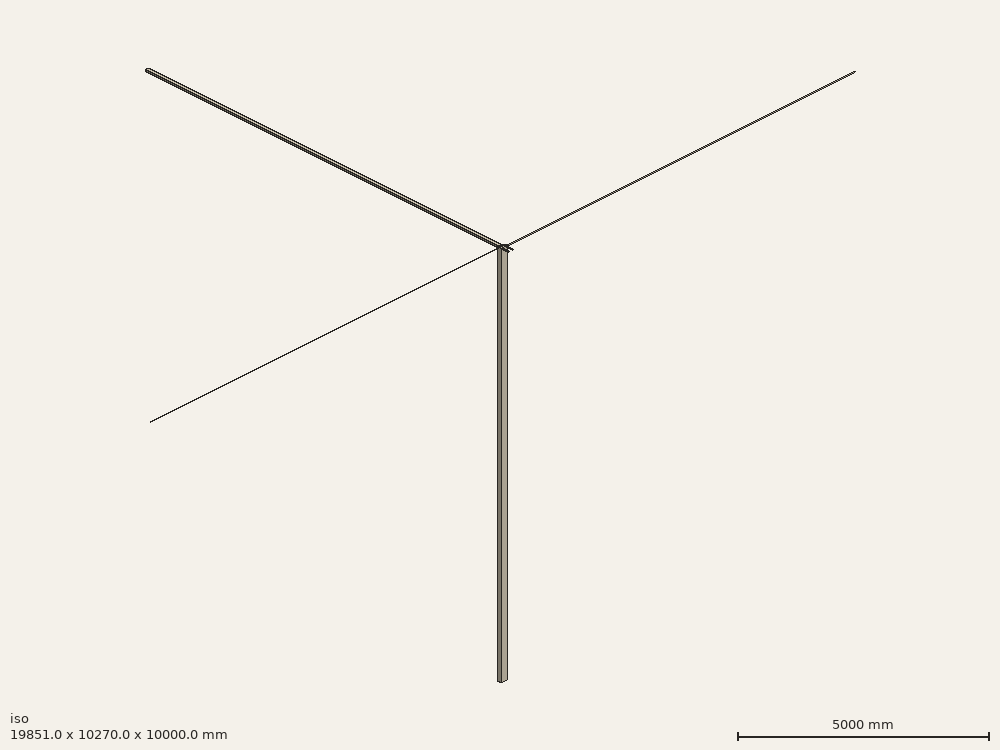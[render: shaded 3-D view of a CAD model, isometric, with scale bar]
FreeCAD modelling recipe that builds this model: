
FCSTD DOCUMENT  (FreeCAD 0.15R4671 (Git))
Label: ZBedBearingCaps
License: All rights reserved
LicenseURL: http://en.wikipedia.org/wiki/All_rights_reserved
objects: Sketcher::SketchObject×27, PartDesign::Pocket×23, Part::Feature×13, Mesh::Feature×9, PartDesign::Pad×4, PartDesign::Chamfer×1, PartDesign::Fillet×1
note: 96 computed .brp shape members not serialized (recipe doc carries the construction recipe); baked Part::Feature solids carry a one-line shape summary decoded from their .brp

FEATURE [Part::Feature] Part__Feature  label="ZRodHolderMiddle001"
  Placement = pos=(0,0,-30) rot=(0,0,1;0rad)
  shape: bbox 156.7 x 50 x 15.66 mm, 189 faces (baked)
FEATURE [Sketcher::SketchObject] Sketch
  sketch-geometry (4):
    g0: LineSegment StartX=-74.5 StartY=-14 StartZ=0 EndX=74.5 EndY=-14 EndZ=0
    g1: LineSegment StartX=74.5 StartY=-14 StartZ=0 EndX=74.5 EndY=-79 EndZ=0
    g2: LineSegment StartX=74.5 StartY=-79 StartZ=0 EndX=-74.5 EndY=-79 EndZ=0
    g3: LineSegment StartX=-74.5 StartY=-79 StartZ=0 EndX=-74.5 EndY=-14 EndZ=0
  constraints (12):
    c: Coincident(g0,g1)
    c: Coincident(g1,g2)
    c: Coincident(g2,g3)
    c: Coincident(g3,g0)
    c: Horizontal(g0)
    c: Horizontal(g2)
    c: Vertical(g1)
    c: Vertical(g3)
    c: DistanceY(g0) = -14
    c: DistanceY(g0,g2) = -65
    c: DistanceX(g-1,g0) = 74.5
    c: DistanceX(g-1,g0) = -74.5
FEATURE [Mesh::Feature] MK2a_Heatbed
  Placement = pos=(0,-185,51.5) rot=(0,0,1;0rad)
FEATURE [Part::Feature] Part__Feature001  label="OB1515_270mm"
  Placement = pos=(-60,-44,42.5) rot=(1,0,0;1.5708rad)
  shape: bbox 15 x 270 x 15 mm, 158 faces (baked)
FEATURE [Part::Feature] Part__Feature002  label="OB1515_270mm001"
  Placement = pos=(60,-44,42.5) rot=(1,0,0;1.5708rad)
  shape: bbox 15 x 270 x 15 mm, 158 faces (baked)
FEATURE [Part::Feature] _mmBrasNut
  Placement = pos=(0,-28.25,40) rot=(0,-1,0;1.5708rad)
  shape: bbox 22 x 22 x 16.42 mm, 29 faces (baked)
FEATURE [Part::Feature] LM8UU_8mm_Linear_Bearing
  Placement = pos=(-60,-28,26) rot=(0,1,0;1.5708rad)
  shape: bbox 15 x 15 x 24 mm, 34 faces (baked)
FEATURE [Part::Feature] LM8UU_8mm_Linear_Bearing001
  Placement = pos=(60,-28,26) rot=(0,1,0;1.5708rad)
  shape: bbox 15 x 15 x 24 mm, 34 faces (baked)
FEATURE [Part::Feature] LM8UU_8mm_Linear_Bearing002
  Placement = pos=(-60,-28,53) rot=(0,1,0;1.5708rad)
  shape: bbox 15 x 15 x 24 mm, 34 faces (baked)
FEATURE [Part::Feature] LM8UU_8mm_Linear_Bearing003
  Placement = pos=(60,-28,53) rot=(0,1,0;1.5708rad)
  shape: bbox 15 x 15 x 24 mm, 34 faces (baked)
FEATURE [PartDesign::Pad] Pad
  Length = 55
  Length2 = 100
  Sketch = -> Sketch
  Type = 0
FEATURE [Sketcher::SketchObject] Sketch001
  Placement = pos=(0,-79,0) rot=(1,0,0;1.5708rad)
  Support = -> Pad [Face3]
  sketch-geometry (8):
    g0: LineSegment StartX=-67.75 StartY=50.25 StartZ=0 EndX=-52.25 EndY=50.25 EndZ=0
    g1: LineSegment StartX=-52.25 StartY=50.25 StartZ=0 EndX=-52.25 EndY=-6 EndZ=0
    g2: LineSegment StartX=-52.25 StartY=-6 StartZ=0 EndX=-67.75 EndY=-6 EndZ=0
    g3: LineSegment StartX=-67.75 StartY=-6 StartZ=0 EndX=-67.75 EndY=50.25 EndZ=0
    g4: LineSegment StartX=52.25 StartY=50.25 StartZ=0 EndX=67.75 EndY=50.25 EndZ=0
    g5: LineSegment StartX=67.75 StartY=50.25 StartZ=0 EndX=67.75 EndY=-6.12629 EndZ=0
    g6: LineSegment StartX=67.75 StartY=-6.12629 StartZ=0 EndX=52.25 EndY=-6.12629 EndZ=0
    g7: LineSegment StartX=52.25 StartY=-6.12629 StartZ=0 EndX=52.25 EndY=50.25 EndZ=0
  constraints (16):
    c: Coincident(g0,g1)
    c: Coincident(g1,g2)
    c: Coincident(g2,g3)
    c: Coincident(g3,g0)
    c: Horizontal(g0)
    c: Horizontal(g2)
    c: Vertical(g1)
    c: Vertical(g3)
    c: Coincident(g4,g5)
    c: Coincident(g5,g6)
    c: Coincident(g6,g7)
    c: Coincident(g7,g4)
    c: Horizontal(g4)
    c: Horizontal(g6)
    c: Vertical(g5)
    c: Vertical(g7)
FEATURE [PartDesign::Pocket] Pocket
  Length = 35
  Sketch = -> Sketch001
  Type = 0
FEATURE [Sketcher::SketchObject] Sketch002
  Placement = pos=(-74.5,0,0) rot=(0.57735,-0.57735,-0.57735;2.0944rad)
  Support = -> Pocket [Face2]
  sketch-geometry (5):
    g0: LineSegment StartX=79.5 StartY=35 StartZ=0 EndX=79 EndY=35 EndZ=0
    g1: LineSegment StartX=79 StartY=35 StartZ=0 EndX=44 EndY=0 EndZ=0
    g2: LineSegment StartX=44 StartY=0 StartZ=0 EndX=44 EndY=-0.5 EndZ=0
    g3: LineSegment StartX=44 StartY=-0.5 StartZ=0 EndX=79.5 EndY=-0.5 EndZ=0
    g4: LineSegment StartX=79.5 StartY=-0.5 StartZ=0 EndX=79.5 EndY=35 EndZ=0
  constraints (10):
    c: Horizontal(g0)
    c: Coincident(g0,g1)
    c: PointOnObject(g1,g-1)
    c: Coincident(g1,g2)
    c: Vertical(g2)
    c: Coincident(g2,g3)
    c: Horizontal(g3)
    c: Coincident(g3,g4)
    c: Coincident(g4,g0)
    c: Vertical(g4)
FEATURE [PartDesign::Pocket] Pocket001
  Length = 5
  Sketch = -> Sketch002
  Type = 1
FEATURE [Sketcher::SketchObject] Sketch003
  Placement = pos=(0,-79,0) rot=(1,0,0;1.5708rad)
  Support = -> Pocket001 [Face7]
  sketch-geometry (4):
    g0: LineSegment StartX=-45 StartY=45 StartZ=0 EndX=45 EndY=45 EndZ=0
    g1: LineSegment StartX=45 StartY=45 StartZ=0 EndX=45 EndY=-2 EndZ=0
    g2: LineSegment StartX=45 StartY=-2 StartZ=0 EndX=-45 EndY=-2 EndZ=0
    g3: LineSegment StartX=-45 StartY=-2 StartZ=0 EndX=-45 EndY=45 EndZ=0
  constraints (8):
    c: Coincident(g0,g1)
    c: Coincident(g1,g2)
    c: Coincident(g2,g3)
    c: Coincident(g3,g0)
    c: Horizontal(g0)
    c: Horizontal(g2)
    c: Vertical(g1)
    c: Vertical(g3)
FEATURE [PartDesign::Pocket] Pocket002
  Length = 35
  Sketch = -> Sketch003
  Type = 0
FEATURE [Sketcher::SketchObject] Sketch005
  Placement = pos=(0,-44,0) rot=(1,0,0;1.5708rad)
  Support = -> Pocket002 [Face13]
  sketch-geometry (4):
    g0: LineSegment StartX=-45 StartY=45 StartZ=0 EndX=45 EndY=45 EndZ=0
    g1: LineSegment StartX=45 StartY=45 StartZ=0 EndX=45 EndY=-2 EndZ=0
    g2: LineSegment StartX=45 StartY=-2 StartZ=0 EndX=-45 EndY=-2 EndZ=0
    g3: LineSegment StartX=-45 StartY=-2 StartZ=0 EndX=-45 EndY=45 EndZ=0
  constraints (8):
    c: Coincident(g0,g1)
    c: Coincident(g1,g2)
    c: Coincident(g2,g3)
    c: Coincident(g3,g0)
    c: Horizontal(g0)
    c: Horizontal(g2)
    c: Vertical(g1)
    c: Vertical(g3)
FEATURE [PartDesign::Pocket] Pocket003
  Length = 5
  Sketch = -> Sketch005
  Type = 1
FEATURE [Sketcher::SketchObject] Sketch006
  Placement = pos=(0,0,55) rot=(0,0,1;0rad)
  Support = -> Pocket003 [Face5]
  sketch-geometry (4):
    g0: LineSegment StartX=-45 StartY=-81 StartZ=0 EndX=-45 EndY=-44 EndZ=0
    g1: LineSegment StartX=-45 StartY=-44 StartZ=0 EndX=45 EndY=-44 EndZ=0
    g2: LineSegment StartX=45 StartY=-44 StartZ=0 EndX=45 EndY=-81 EndZ=0
    g3: LineSegment StartX=45 StartY=-81 StartZ=0 EndX=-45 EndY=-81 EndZ=0
  constraints (4):
    c: Coincident(g0,g1)
    c: Coincident(g1,g2)
    c: Coincident(g2,g3)
    c: Coincident(g3,g0)
FEATURE [PartDesign::Pocket] Pocket004
  Length = 5
  Sketch = -> Sketch006
  Type = 1
FEATURE [Sketcher::SketchObject] Sketch007
  Placement = pos=(0,0,55) rot=(0,0,1;0rad)
  Support = -> Pocket004 [Face6]
  sketch-geometry (1):
    g0: Circle CenterX=0 CenterY=-28.2788 CenterZ=0 NormalX=0 NormalY=0 NormalZ=1 Radius=5.50059
FEATURE [PartDesign::Pocket] Pocket005
  Length = 5
  Sketch = -> Sketch007
  Type = 1
FEATURE [Sketcher::SketchObject] Sketch008
  Placement = pos=(0,0,55) rot=(0,0,1;0rad)
  Support = -> Pocket005 [Face8]
  sketch-geometry (4):
    g0: Circle CenterX=0 CenterY=-36.25 CenterZ=0 NormalX=0 NormalY=0 NormalZ=1 Radius=1.5
    g1: Circle CenterX=0 CenterY=-20.25 CenterZ=0 NormalX=0 NormalY=0 NormalZ=1 Radius=1.5
    g2: Circle CenterX=8 CenterY=-28.25 CenterZ=0 NormalX=0 NormalY=0 NormalZ=1 Radius=1.5
    g3: Circle CenterX=-8 CenterY=-28.25 CenterZ=0 NormalX=0 NormalY=0 NormalZ=1 Radius=1.5
  constraints (4):
    c: Radius(g3) = 1.5
    c: Equal(g3,g1)
    c: Equal(g3,g2)
    c: Equal(g3,g0)
FEATURE [PartDesign::Pocket] Pocket006
  Length = 5
  Sketch = -> Sketch008
  Type = 1
FEATURE [Sketcher::SketchObject] Sketch009
  Placement = pos=(0,0,55) rot=(0,0,1;0rad)
  Support = -> Pocket006 [Face8]
  sketch-geometry (2):
    g0: Circle CenterX=60 CenterY=-28 CenterZ=0 NormalX=0 NormalY=0 NormalZ=1 Radius=7.75
    g1: Circle CenterX=-60 CenterY=-28 CenterZ=0 NormalX=0 NormalY=0 NormalZ=1 Radius=7.75
  constraints (2):
    c: Radius(g1) = 7.75
    c: Equal(g1,g0)
FEATURE [PartDesign::Pocket] Pocket007
  Length = 26.75
  Sketch = -> Sketch009
  Type = 0
FEATURE [Sketcher::SketchObject] Sketch010
  Placement = pos=(0,0,0) rot=(1,0,0;3.14159rad)
  Support = -> Pocket007 [Face2]
  sketch-geometry (2):
    g0: Circle CenterX=-60 CenterY=28 CenterZ=0 NormalX=0 NormalY=0 NormalZ=1 Radius=7.75
    g1: Circle CenterX=60 CenterY=28 CenterZ=0 NormalX=0 NormalY=0 NormalZ=1 Radius=7.75
  constraints (2):
    c: Radius(g0) = 7.75
    c: Equal(g0,g1)
FEATURE [PartDesign::Pocket] Pocket008
  Length = 26.75
  Sketch = -> Sketch010
  Type = 0
FEATURE [Sketcher::SketchObject] Sketch011
  Placement = pos=(0,0,0) rot=(1,0,0;3.14159rad)
  Support = -> Pocket008 [Face2]
  sketch-geometry (8):
    g0: LineSegment StartX=50 StartY=38 StartZ=0 EndX=70 EndY=38 EndZ=0
    g1: LineSegment StartX=70 StartY=38 StartZ=0 EndX=70 EndY=18 EndZ=0
    g2: LineSegment StartX=70 StartY=18 StartZ=0 EndX=50 EndY=18 EndZ=0
    g3: LineSegment StartX=50 StartY=18 StartZ=0 EndX=50 EndY=38 EndZ=0
    g4: LineSegment StartX=-50 StartY=38 StartZ=0 EndX=-70 EndY=38 EndZ=0
    g5: LineSegment StartX=-70 StartY=38 StartZ=0 EndX=-70 EndY=17.9245 EndZ=0
    g6: LineSegment StartX=-70 StartY=17.9245 StartZ=0 EndX=-50 EndY=17.9245 EndZ=0
    g7: LineSegment StartX=-50 StartY=17.9245 StartZ=0 EndX=-50 EndY=38 EndZ=0
  constraints (16):
    c: Coincident(g0,g1)
    c: Coincident(g1,g2)
    c: Coincident(g2,g3)
    c: Coincident(g3,g0)
    c: Horizontal(g0)
    c: Horizontal(g2)
    c: Vertical(g1)
    c: Vertical(g3)
    c: Coincident(g4,g5)
    c: Coincident(g5,g6)
    c: Coincident(g6,g7)
    c: Coincident(g7,g4)
    c: Horizontal(g4)
    c: Horizontal(g6)
    c: Vertical(g5)
    c: Vertical(g7)
FEATURE [PartDesign::Pad] Pad001
  Length = 1.25
  Length2 = 100
  Reversed = true
  Sketch = -> Sketch011
  Type = 0
FEATURE [Sketcher::SketchObject] Sketch012
  Placement = pos=(0,0,55) rot=(0,0,1;0rad)
  Support = -> Pad001 [Face6]
  sketch-geometry (8):
    g0: LineSegment StartX=-50 StartY=-18 StartZ=0 EndX=-70 EndY=-18 EndZ=0
    g1: LineSegment StartX=-70 StartY=-18 StartZ=0 EndX=-70 EndY=-38 EndZ=0
    g2: LineSegment StartX=-70 StartY=-38 StartZ=0 EndX=-50 EndY=-38 EndZ=0
    g3: LineSegment StartX=-50 StartY=-38 StartZ=0 EndX=-50 EndY=-18 EndZ=0
    g4: LineSegment StartX=50 StartY=-18 StartZ=0 EndX=70 EndY=-18 EndZ=0
    g5: LineSegment StartX=70 StartY=-18 StartZ=0 EndX=70 EndY=-38 EndZ=0
    g6: LineSegment StartX=70 StartY=-38 StartZ=0 EndX=50 EndY=-38 EndZ=0
    g7: LineSegment StartX=50 StartY=-38 StartZ=0 EndX=50 EndY=-18 EndZ=0
  constraints (16):
    c: Coincident(g0,g1)
    c: Coincident(g1,g2)
    c: Coincident(g2,g3)
    c: Coincident(g3,g0)
    c: Horizontal(g0)
    c: Horizontal(g2)
    c: Vertical(g1)
    c: Vertical(g3)
    c: Coincident(g4,g5)
    c: Coincident(g5,g6)
    c: Coincident(g6,g7)
    c: Coincident(g7,g4)
    c: Horizontal(g4)
    c: Horizontal(g6)
    c: Vertical(g5)
    c: Vertical(g7)
FEATURE [PartDesign::Pad] Pad002
  Length = 1.25
  Length2 = 100
  Reversed = true
  Sketch = -> Sketch012
  Type = 0
FEATURE [Part::Feature] Pad002001  label="Pad003"
  shape: bbox 149 x 65 x 55 mm, 41 faces (baked)
FEATURE [Sketcher::SketchObject] Sketch013
  Placement = pos=(0,0,55) rot=(0,0,1;0rad)
  Support = -> Pad002001 [Face29]
  sketch-geometry (2):
    g0: Circle CenterX=60 CenterY=-28 CenterZ=0 NormalX=0 NormalY=0 NormalZ=1 Radius=6
    g1: Circle CenterX=-60 CenterY=-28 CenterZ=0 NormalX=0 NormalY=0 NormalZ=1 Radius=6
  constraints (2):
    c: Radius(g0) = 6
    c: Equal(g0,g1)
FEATURE [PartDesign::Pocket] Pocket009
  Length = 5
  Sketch = -> Sketch013
  Type = 1
FEATURE [Mesh::Feature] HexNutStyle1_M3
  Placement = pos=(-47,-148,15) rot=(-0.935113,0.250563,0.250563;1.63783rad)
FEATURE [Mesh::Feature] HexNutStyle1_M
  Placement = pos=(-70,-148,15) rot=(-0.935113,0.250563,0.250563;1.63783rad)
FEATURE [Mesh::Feature] HexNutStyle1_M004
  Placement = pos=(72.5,-148,15) rot=(-0.935113,0.250563,0.250563;1.63783rad)
FEATURE [Mesh::Feature] HexNutStyle1_M005
  Placement = pos=(49.5,-148,15) rot=(-0.935113,0.250563,0.250563;1.63783rad)
FEATURE [Mesh::Feature] HexNutStyle1_M006
  Placement = pos=(-47,-148,-12) rot=(-0.935113,0.250563,0.250563;1.63783rad)
FEATURE [Mesh::Feature] HexNutStyle1_M007
  Placement = pos=(-70,-148,-12) rot=(-0.935113,0.250563,0.250563;1.63783rad)
FEATURE [Mesh::Feature] HexNutStyle1_M008
  Placement = pos=(72.5,-148,-12) rot=(-0.935113,0.250563,0.250563;1.63783rad)
FEATURE [Mesh::Feature] HexNutStyle1_M009
  Placement = pos=(49.5,-148,-12) rot=(-0.935113,0.250563,0.250563;1.63783rad)
FEATURE [Sketcher::SketchObject] Sketch014
  Placement = pos=(0,-14,0) rot=(0,0.707107,0.707107;3.14159rad)
  Support = -> Pocket009 [Face1]
  sketch-geometry (8):
    g0: Circle CenterX=48.3004 CenterY=41.1597 CenterZ=0 NormalX=0 NormalY=0 NormalZ=1 Radius=1.8
    g1: Circle CenterX=71.3061 CenterY=41.157 CenterZ=0 NormalX=0 NormalY=0 NormalZ=1 Radius=1.8
    g2: Circle CenterX=71.2993 CenterY=14.1443 CenterZ=0 NormalX=0 NormalY=0 NormalZ=1 Radius=1.8
    g3: Circle CenterX=48.2996 CenterY=14.1465 CenterZ=0 NormalX=0 NormalY=0 NormalZ=1 Radius=1.8
    g4: Circle CenterX=-48.2006 CenterY=41.1589 CenterZ=0 NormalX=0 NormalY=0 NormalZ=1 Radius=1.8
    g5: Circle CenterX=-71.2074 CenterY=41.1588 CenterZ=0 NormalX=0 NormalY=0 NormalZ=1 Radius=1.8
    g6: Circle CenterX=-48.2029 CenterY=14.1601 CenterZ=0 NormalX=0 NormalY=0 NormalZ=1 Radius=1.8
    g7: Circle CenterX=-71.1962 CenterY=14.1573 CenterZ=0 NormalX=0 NormalY=0 NormalZ=1 Radius=1.8
  constraints (2):
    c: Radius(g0) = 1.8
    c: Equal(g0, g1-g7) x7
FEATURE [PartDesign::Pocket] Pocket010
  Length = 28
  Sketch = -> Sketch014
  Type = 0
FEATURE [Sketcher::SketchObject] Sketch017
  Placement = pos=(0,0,55) rot=(0,0,1;0rad)
  Support = -> Pocket010 [Face5]
  sketch-geometry (21):
    g0: LineSegment StartX=74 StartY=-43.5 StartZ=0 EndX=74.5 EndY=-44 EndZ=0
    g1: LineSegment StartX=74.5 StartY=-44 StartZ=0 EndX=76.5 EndY=-42 EndZ=0
    g2: LineSegment StartX=76.5 StartY=-42 StartZ=0 EndX=76.5 EndY=-14 EndZ=0
    g3: LineSegment StartX=76.5 StartY=-14 StartZ=0 EndX=74 EndY=-14 EndZ=0
    g4: LineSegment StartX=74 StartY=-14 StartZ=0 EndX=74 EndY=-43.1086 EndZ=0
    g5: LineSegment StartX=74 StartY=-43.1086 StartZ=0 EndX=74 EndY=-43.5 EndZ=0
    g6: LineSegment StartX=-74 StartY=-44 StartZ=0 EndX=-74.5 EndY=-44 EndZ=0
    g7: LineSegment StartX=-74.5 StartY=-44 StartZ=0 EndX=-76.5 EndY=-42 EndZ=0
    g8: LineSegment StartX=-76.5 StartY=-42 StartZ=0 EndX=-76.5 EndY=-14 EndZ=0
    g9: LineSegment StartX=-76.5 StartY=-14 StartZ=0 EndX=-74 EndY=-14 EndZ=0
    g10: LineSegment StartX=-74 StartY=-14 StartZ=0 EndX=-74 EndY=-44 EndZ=0
    g11: LineSegment StartX=-45.5 StartY=-44 StartZ=0 EndX=-45 EndY=-44 EndZ=0
    g12: LineSegment StartX=-45 StartY=-44 StartZ=0 EndX=-43 EndY=-42 EndZ=0
    g13: LineSegment StartX=-43 StartY=-42 StartZ=0 EndX=-43 EndY=-14 EndZ=0
    g14: LineSegment StartX=-43 StartY=-14 StartZ=0 EndX=-45.5 EndY=-14 EndZ=0
    g15: LineSegment StartX=-45.5 StartY=-14 StartZ=0 EndX=-45.5 EndY=-44 EndZ=0
    g16: LineSegment StartX=45.5 StartY=-44 StartZ=0 EndX=45 EndY=-44 EndZ=0
    g17: LineSegment StartX=45 StartY=-44 StartZ=0 EndX=43 EndY=-42 EndZ=0
    g18: LineSegment StartX=43 StartY=-42 StartZ=0 EndX=43 EndY=-14 EndZ=0
    g19: LineSegment StartX=43 StartY=-14 StartZ=0 EndX=45.5 EndY=-14 EndZ=0
    g20: LineSegment StartX=45.5 StartY=-14 StartZ=0 EndX=45.5 EndY=-44 EndZ=0
  constraints (21):
    c: Coincident(g0,g1)
    c: Coincident(g1,g2)
    c: Coincident(g2,g3)
    c: Coincident(g3,g4)
    c: Coincident(g4,g5)
    c: Coincident(g5,g0)
    c: Coincident(g6,g7)
    c: Coincident(g7,g8)
    c: Coincident(g8,g9)
    c: Coincident(g9,g10)
    c: Coincident(g10,g6)
    c: Coincident(g11,g12)
    c: Coincident(g12,g13)
    c: Coincident(g13,g14)
    c: Coincident(g14,g15)
    c: Coincident(g15,g11)
    c: Coincident(g16,g17)
    c: Coincident(g17,g18)
    c: Coincident(g18,g19)
    c: Coincident(g19,g20)
    c: Coincident(g20,g16)
FEATURE [PartDesign::Pad] Pad002002
  Length = 55
  Length2 = 100
  Reversed = true
  Sketch = -> Sketch017
  Type = 0
FEATURE [Part::Feature] Pad002003
  shape: bbox 153 x 65 x 55 mm, 71 faces (baked)
FEATURE [Sketcher::SketchObject] Sketch018
  Placement = pos=(0,-14,0) rot=(0,0.707107,0.707107;3.14159rad)
  Support = -> Pad002003 [Face34]
  sketch-geometry (8):
    g0: Circle CenterX=-71.1996 CenterY=41.1697 CenterZ=0 NormalX=0 NormalY=0 NormalZ=1 Radius=3.4
    g1: Circle CenterX=-48.1947 CenterY=41.1566 CenterZ=0 NormalX=0 NormalY=0 NormalZ=1 Radius=3.4
    g2: Circle CenterX=-71.196 CenterY=14.1515 CenterZ=0 NormalX=0 NormalY=0 NormalZ=1 Radius=3.4
    g3: Circle CenterX=-48.1951 CenterY=14.1668 CenterZ=0 NormalX=0 NormalY=0 NormalZ=1 Radius=3.4
    g4: Circle CenterX=48.2953 CenterY=41.166 CenterZ=0 NormalX=0 NormalY=0 NormalZ=1 Radius=3.4
    g5: Circle CenterX=71.309 CenterY=41.1689 CenterZ=0 NormalX=0 NormalY=0 NormalZ=1 Radius=3.4
    g6: Circle CenterX=71.2966 CenterY=14.1495 CenterZ=0 NormalX=0 NormalY=0 NormalZ=1 Radius=3.4
    g7: Circle CenterX=48.296 CenterY=14.1509 CenterZ=0 NormalX=0 NormalY=0 NormalZ=1 Radius=3.4
  constraints (2):
    c: Radius(g0) = 3.4
    c: Equal(g0, g1-g7) x7
FEATURE [PartDesign::Pocket] Pocket011
  Length = 12
  Sketch = -> Sketch018
  Type = 0
FEATURE [Sketcher::SketchObject] Sketch019
  Placement = pos=(0,0,55) rot=(0,0,1;0rad)
  Support = -> Pocket011 [Face11]
  sketch-geometry (6):
    g0: LineSegment StartX=-43 StartY=-12 StartZ=0 EndX=-43 EndY=-28 EndZ=0
    g1: LineSegment StartX=-43 StartY=-28 StartZ=0 EndX=-14 EndY=-28 EndZ=0
    g2: ArcOfCircle CenterX=0 CenterY=-28 CenterZ=0 NormalX=0 NormalY=0 NormalZ=1 Radius=14 StartAngle=0 EndAngle=3.14159
    g3: LineSegment StartX=-43 StartY=-12 StartZ=0 EndX=43 EndY=-12 EndZ=0
    g4: LineSegment StartX=43 StartY=-12 StartZ=0 EndX=43 EndY=-28 EndZ=0
    g5: LineSegment StartX=43 StartY=-28 StartZ=0 EndX=14 EndY=-28 EndZ=0
  constraints (6):
    c: Coincident(g0,g1)
    c: Coincident(g1,g2)
    c: Coincident(g3,g4)
    c: Coincident(g4,g5)
    c: Coincident(g2,g5)
    c: Coincident(g0,g3)
FEATURE [PartDesign::Pocket] Pocket012
  Length = 5
  Sketch = -> Sketch019
  Type = 1
FEATURE [PartDesign::Chamfer] Chamfer
  Base = -> Pocket012 [Edge138,Edge141]
  Size = 11
FEATURE [Sketcher::SketchObject] Sketch020
  Placement = pos=(0,0,55) rot=(0,0,1;0rad)
  Support = -> Chamfer [Face9]
  sketch-geometry (20):
    g0: LineSegment StartX=41 StartY=-16 StartZ=0 EndX=43 EndY=-16 EndZ=0
    g1: LineSegment StartX=43 StartY=-16 StartZ=0 EndX=45 EndY=-14 EndZ=0
    g2: LineSegment StartX=45 StartY=-14 StartZ=0 EndX=45 EndY=-12 EndZ=0
    g3: LineSegment StartX=45 StartY=-12 StartZ=0 EndX=41 EndY=-12 EndZ=0
    g4: LineSegment StartX=41 StartY=-12 StartZ=0 EndX=41 EndY=-16 EndZ=0
    g5: LineSegment StartX=74.5004 StartY=-12 StartZ=0 EndX=74.5004 EndY=-14 EndZ=0
    g6: LineSegment StartX=74.5004 StartY=-14 StartZ=0 EndX=76.5 EndY=-16 EndZ=0
    g7: LineSegment StartX=76.5 StartY=-16 StartZ=0 EndX=78 EndY=-16 EndZ=0
    g8: LineSegment StartX=78 StartY=-16 StartZ=0 EndX=78 EndY=-12 EndZ=0
    g9: LineSegment StartX=78 StartY=-12 StartZ=0 EndX=74.5004 EndY=-12 EndZ=0
    g10: LineSegment StartX=-45 StartY=-13.5 StartZ=0 EndX=-45 EndY=-14 EndZ=0
    g11: LineSegment StartX=-45 StartY=-14 StartZ=0 EndX=-43 EndY=-16 EndZ=0
    g12: LineSegment StartX=-43 StartY=-16 StartZ=0 EndX=-42.5 EndY=-16 EndZ=0
    g13: LineSegment StartX=-42.5 StartY=-16 StartZ=0 EndX=-42.5 EndY=-13.5 EndZ=0
    g14: LineSegment StartX=-42.5 StartY=-13.5 StartZ=0 EndX=-45 EndY=-13.5 EndZ=0
    g15: LineSegment StartX=-77.5 StartY=-13 StartZ=0 EndX=-74.5 EndY=-13 EndZ=0
    g16: LineSegment StartX=-74.5 StartY=-13 StartZ=0 EndX=-74.5 EndY=-14 EndZ=0
    g17: LineSegment StartX=-74.5 StartY=-14 StartZ=0 EndX=-76.5 EndY=-16 EndZ=0
    g18: LineSegment StartX=-76.5 StartY=-16 StartZ=0 EndX=-77.5 EndY=-16 EndZ=0
    g19: LineSegment StartX=-77.5 StartY=-16 StartZ=0 EndX=-77.5 EndY=-13 EndZ=0
  constraints (20):
    c: Coincident(g0,g1)
    c: Coincident(g1,g2)
    c: Coincident(g2,g3)
    c: Coincident(g3,g4)
    c: Coincident(g4,g0)
    c: Coincident(g5,g6)
    c: Coincident(g6,g7)
    c: Coincident(g7,g8)
    c: Coincident(g8,g9)
    c: Coincident(g9,g5)
    c: Coincident(g10,g11)
    c: Coincident(g11,g12)
    c: Coincident(g12,g13)
    c: Coincident(g13,g14)
    c: Coincident(g14,g10)
    c: Coincident(g15,g16)
    c: Coincident(g16,g17)
    c: Coincident(g17,g18)
    c: Coincident(g18,g19)
    c: Coincident(g19,g15)
FEATURE [PartDesign::Pocket] Pocket013
  Length = 5
  Sketch = -> Sketch020
  Type = 1
FEATURE [Sketcher::SketchObject] Sketch021
  Placement = pos=(0,0,55) rot=(0,0,1;0rad)
  Support = -> Pocket013 [Face8]
  sketch-geometry (4):
    g0: Circle CenterX=60 CenterY=-72.5 CenterZ=0 NormalX=0 NormalY=0 NormalZ=1 Radius=1.8
    g1: Circle CenterX=-60 CenterY=-72.5 CenterZ=0 NormalX=0 NormalY=0 NormalZ=1 Radius=1.8
    g2: Circle CenterX=-60 CenterY=-50 CenterZ=0 NormalX=0 NormalY=0 NormalZ=1 Radius=1.8
    g3: Circle CenterX=60 CenterY=-50 CenterZ=0 NormalX=0 NormalY=0 NormalZ=1 Radius=1.8
  constraints (4):
    c: Radius(g0) = 1.8
    c: Equal(g0,g1)
    c: Equal(g0,g2)
    c: Equal(g0,g3)
FEATURE [PartDesign::Pocket] Pocket014
  Length = 5
  Sketch = -> Sketch021
  Type = 1
FEATURE [Sketcher::SketchObject] Sketch022
  Placement = pos=(0,0,55) rot=(0,0,1;0rad)
  Support = -> Pocket014 [Face8]
  sketch-geometry (4):
    g0: Circle CenterX=60 CenterY=-50 CenterZ=0 NormalX=0 NormalY=0 NormalZ=1 Radius=3.6
    g1: Circle CenterX=60 CenterY=-72.5 CenterZ=0 NormalX=0 NormalY=0 NormalZ=1 Radius=3.6
    g2: Circle CenterX=-60 CenterY=-50 CenterZ=0 NormalX=0 NormalY=0 NormalZ=1 Radius=3.6
    g3: Circle CenterX=-60 CenterY=-72.5 CenterZ=0 NormalX=0 NormalY=0 NormalZ=1 Radius=3.6
  constraints (4):
    c: Radius(g0) = 3.6
    c: Equal(g0,g1)
    c: Equal(g0,g2)
    c: Equal(g0,g3)
FEATURE [PartDesign::Pocket] Pocket015
  Length = 3
  Sketch = -> Sketch022
  Type = 0
FEATURE [Sketcher::SketchObject] Sketch023
  Placement = pos=(74.5,0,0) rot=(0.57735,0.57735,0.57735;2.0944rad)
  Support = -> Pocket015 [Face35]
  sketch-geometry (2):
    g0: Circle CenterX=-72.5 CenterY=42.5 CenterZ=0 NormalX=0 NormalY=0 NormalZ=1 Radius=1.8
    g1: Circle CenterX=-50 CenterY=42.5 CenterZ=0 NormalX=0 NormalY=0 NormalZ=1 Radius=1.8
  constraints (2):
    c: Radius(g0) = 1.8
    c: Equal(g0,g1)
FEATURE [PartDesign::Pocket] Pocket016
  Length = 5
  Sketch = -> Sketch023
  Type = 1
FEATURE [Sketcher::SketchObject] Sketch024
  Placement = pos=(74.5,0,0) rot=(0.57735,0.57735,0.57735;2.0944rad)
  Support = -> Pocket016 [Face37]
  sketch-geometry (2):
    g0: Circle CenterX=-50 CenterY=42.5 CenterZ=0 NormalX=0 NormalY=0 NormalZ=1 Radius=3.6
    g1: Circle CenterX=-72.5 CenterY=42.5 CenterZ=0 NormalX=0 NormalY=0 NormalZ=1 Radius=3.6
  constraints (2):
    c: Radius(g1) = 3.6
    c: Equal(g1,g0)
FEATURE [PartDesign::Pocket] Pocket017
  Length = 3
  Sketch = -> Sketch024
  Type = 0
FEATURE [Sketcher::SketchObject] Sketch025
  Placement = pos=(45,0,0) rot=(0.57735,-0.57735,-0.57735;2.0944rad)
  Support = -> Pocket017 [Face33]
  sketch-geometry (2):
    g0: Circle CenterX=50 CenterY=42.5 CenterZ=0 NormalX=0 NormalY=0 NormalZ=1 Radius=3.6
    g1: Circle CenterX=72.5 CenterY=42.5 CenterZ=0 NormalX=0 NormalY=0 NormalZ=1 Radius=3.6
  constraints (2):
    c: Radius(g0) = 3.6
    c: Equal(g0,g1)
FEATURE [PartDesign::Pocket] Pocket018
  Length = 3
  Sketch = -> Sketch025
  Type = 0
FEATURE [Sketcher::SketchObject] Sketch026
  Placement = pos=(-45,0,0) rot=(0.57735,0.57735,0.57735;2.0944rad)
  Support = -> Pocket018 [Face6]
  sketch-geometry (2):
    g0: Circle CenterX=-50 CenterY=42.5 CenterZ=0 NormalX=0 NormalY=0 NormalZ=1 Radius=3.6
    g1: Circle CenterX=-72.5 CenterY=42.5 CenterZ=0 NormalX=0 NormalY=0 NormalZ=1 Radius=3.6
  constraints (2):
    c: Radius(g0) = 3.6
    c: Equal(g0,g1)
FEATURE [PartDesign::Pocket] Pocket019
  Length = 3
  Sketch = -> Sketch026
  Type = 0
FEATURE [Sketcher::SketchObject] Sketch027
  Placement = pos=(-74.5,0,0) rot=(0.57735,-0.57735,-0.57735;2.0944rad)
  Support = -> Pocket019 [Face31]
  sketch-geometry (2):
    g0: Circle CenterX=50 CenterY=42.5 CenterZ=0 NormalX=0 NormalY=0 NormalZ=1 Radius=3.6
    g1: Circle CenterX=72.5 CenterY=42.5 CenterZ=0 NormalX=0 NormalY=0 NormalZ=1 Radius=3.6
  constraints (2):
    c: Radius(g0) = 3.6
    c: Equal(g0,g1)
FEATURE [PartDesign::Pocket] Pocket020
  Length = 3
  Sketch = -> Sketch027
  Type = 0
FEATURE [Part::Feature] Pocket021
  shape: bbox 153 x 65 x 55 mm, 133 faces (baked)
FEATURE [PartDesign::Fillet] Fillet
  Base = -> Pocket021 [Edge107,Edge102,Edge161,Edge163]
  Radius = 4
FEATURE [Part::Feature] Fillet001
  shape: bbox 153 x 65 x 55 mm, 137 faces (baked)
FEATURE [Part::Feature] Fillet001_solid  label="Fillet001 (Solid)"
  shape: bbox 153 x 65 x 55 mm, 137 faces (baked)
FEATURE [Sketcher::SketchObject] Sketch028
  Placement = pos=(0,0,55) rot=(0,0,1;0rad)
  Support = -> Fillet001_solid [Face7]
  sketch-geometry (7):
    g0: LineSegment StartX=-77.5 StartY=-27.5 StartZ=0 EndX=-42.5 EndY=-27.5 EndZ=0
    g1: LineSegment StartX=-42.5 StartY=-27.5 StartZ=0 EndX=0 EndY=-10.5 EndZ=0
    g2: LineSegment StartX=0 StartY=-10.5 StartZ=0 EndX=42.5 EndY=-27.5 EndZ=0
    g3: LineSegment StartX=42.5 StartY=-27.5 StartZ=0 EndX=77.5 EndY=-27.5 EndZ=0
    g4: LineSegment StartX=77.5 StartY=-27.5 StartZ=0 EndX=77.5 EndY=-83.5 EndZ=0
    g5: LineSegment StartX=77.5 StartY=-83.5 StartZ=0 EndX=-77.5 EndY=-83.5 EndZ=0
    g6: LineSegment StartX=-77.5 StartY=-83.5 StartZ=0 EndX=-77.5 EndY=-27.5 EndZ=0
  constraints (12):
    c: Coincident(g0,g1)
    c: Coincident(g1,g2)
    c: Coincident(g2,g3)
    c: Coincident(g3,g4)
    c: Coincident(g4,g5)
    c: Coincident(g5,g6)
    c: Coincident(g6,g0)
    c: Vertical(g6)
    c: Vertical(g4)
    c: Horizontal(g0)
    c: Horizontal(g3)
    c: Horizontal(g5)
FEATURE [PartDesign::Pocket] Pocket022  label="ZBedBearingCapL"
  Length = 5
  Sketch = -> Sketch028
  Type = 1
FEATURE [Sketcher::SketchObject] Sketch029
  Placement = pos=(0,0,55) rot=(0,0,1;0rad)
  Support = -> Fillet001_solid [Face7]
  sketch-geometry (6):
    g0: LineSegment StartX=37 StartY=-27.5 StartZ=0 EndX=78.5 EndY=-27.5 EndZ=0
    g1: LineSegment StartX=78.5 StartY=-27.5 StartZ=0 EndX=78.5 EndY=-109 EndZ=0
    g2: LineSegment StartX=78.5 StartY=-109 StartZ=0 EndX=-82.5 EndY=-109 EndZ=0
    g3: LineSegment StartX=-82.5 StartY=-109 StartZ=0 EndX=-82.5 EndY=4.28034 EndZ=0
    g4: LineSegment StartX=-82.5 StartY=4.28034 StartZ=0 EndX=37 EndY=4.28034 EndZ=0
    g5: LineSegment StartX=37 StartY=4.28034 StartZ=0 EndX=37 EndY=-27.5 EndZ=0
  constraints (12):
    c: Coincident(g0,g1)
    c: Coincident(g1,g2)
    c: Coincident(g2,g3)
    c: Coincident(g3,g4)
    c: Coincident(g4,g5)
    c: Coincident(g5,g0)
    c: Vertical(g1)
    c: Vertical(g3)
    c: Horizontal(g4)
    c: Horizontal(g2)
    c: Horizontal(g0)
    c: Vertical(g5)
FEATURE [PartDesign::Pocket] Pocket023  label="ZBedBearingCapR"
  Length = 5
  Sketch = -> Sketch029
  Type = 1
